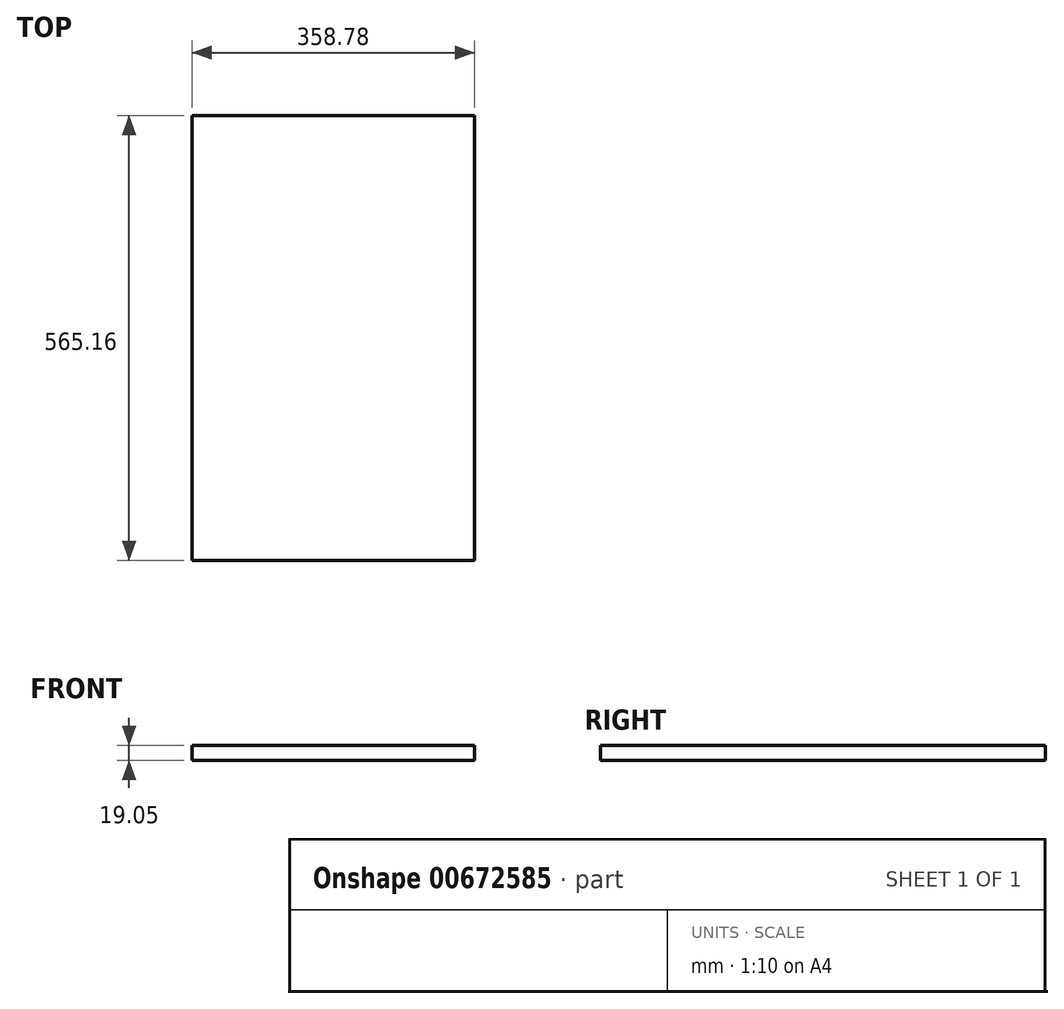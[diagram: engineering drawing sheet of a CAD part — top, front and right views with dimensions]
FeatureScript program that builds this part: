
annotation { "Feature Type Name" : "Feature", "Feature Type Description" : "" }
export const myFeature = defineFeature(function(context is Context, id is Id, definition is map)
    precondition{}
    {
        {
            var Q0;
            Q0=qCreatedBy(makeId("Top.planeOp"),FACE);
            var sketch = newSketch(context, id + "F0", { "sketchPlane" : qUnion([Q0])});
            skLineSegment(sketch, "E0.bottom", {"start": v(179.39, 282.58) * mm, "end": v(-179.39, 282.58) * mm});
            skLineSegment(sketch, "E0.top", {"start": v(179.39, -282.58) * mm, "end": v(-179.39, -282.58) * mm});
            skLineSegment(sketch, "E0.left", {"start": v(179.39, 282.58) * mm, "end": v(179.39, -282.58) * mm});
            skLineSegment(sketch, "E0.right", {"start": v(-179.39, 282.58) * mm, "end": v(-179.39, -282.58) * mm});
            skPoint(sketch, "E0.middle", {"position": v(0, 0) * mm});
            skSolve(sketch);
        }
        {
            var Q0;
            Q0=makeQuery(id+"F0.imprint","IMPRINT",FACE,{"disambiguationData":[TD([[makeQuery(id+"F0.imprint","IMPRINT",EDGE,{"derivedFrom":sQuery(id+"F0.wireOp",EDGE,"E0.bottom")}),1.0]])]});
            extrude(context, id + "F1", {"entities" : qUnion([Q0]), "depth" : 19.05 * mm, "offsetDistance" : 25.4 * mm});
        }
    });
